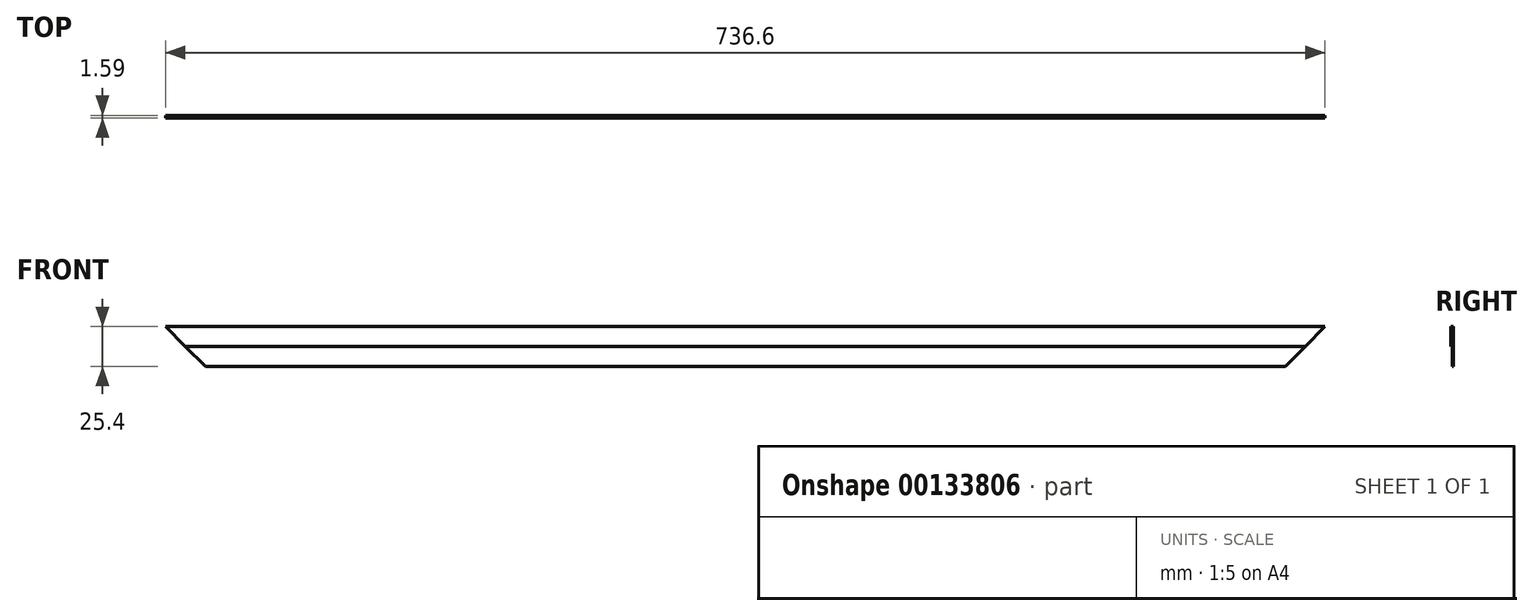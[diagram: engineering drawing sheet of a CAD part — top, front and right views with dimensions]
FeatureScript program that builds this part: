
annotation { "Feature Type Name" : "Feature", "Feature Type Description" : "" }
export const myFeature = defineFeature(function(context is Context, id is Id, definition is map)
    precondition{}
    {
        {
            var Q0;
            Q0=qCreatedBy(makeId("Front.planeOp"),FACE);
            var sketch = newSketch(context, id + "F0", { "sketchPlane" : qUnion([Q0])});
            skLineSegment(sketch, "E0", {"start": v(-25.4, 25.4) * mm, "end": v(711.2, 25.4) * mm});
            skLineSegment(sketch, "E1", {"start": v(711.2, 25.4) * mm, "end": v(685.8, 0) * mm});
            skLineSegment(sketch, "E2", {"start": v(685.8, 0) * mm, "end": v(0, 0) * mm});
            skLineSegment(sketch, "E3", {"start": v(0, 0) * mm, "end": v(-25.4, 25.4) * mm});
            skSolve(sketch);
        }
        {
            var Q0;
            Q0 = qSketchRegion(id + "F0", true);
            extrude(context, id + "F1", {"entities" : qUnion([Q0]), "depth" : 1.59 * mm});
        }
        {
            var Q0;
            Q0=makeQuery(id+"F1.opExtrude","CAP_FACE",FACE,{"disambiguationData":[OSD([sQuery(id+"F0.wireOp",EDGE,"E0"),sQuery(id+"F0.wireOp",EDGE,"E1"),sQuery(id+"F0.wireOp",EDGE,"E2"),sQuery(id+"F0.wireOp",EDGE,"E3")])],"isStart":false});
            var sketch = newSketch(context, id + "F2", { "sketchPlane" : qUnion([Q0])});
            skLineSegment(sketch, "E4", {"start": v(0, 0) * mm, "end": v(-12.7, 12.7) * mm});
            skLineSegment(sketch, "E5", {"start": v(-12.7, 12.7) * mm, "end": v(698.5, 12.7) * mm});
            skLineSegment(sketch, "E6", {"start": v(698.5, 12.7) * mm, "end": v(685.8, 0) * mm});
            skLineSegment(sketch, "E7", {"start": v(685.8, 0) * mm, "end": v(0, 0) * mm});
            skSolve(sketch);
        }
        {
            var Q0;
            Q0 = qSketchRegion(id + "F2", true);
            extrude(context, id + "F3", {"entities" : qUnion([Q0]), "operationType" : NewBodyOperationType.REMOVE, "oppositeDirection" : true, "depth" : 0.8 * mm});
        }
    });
